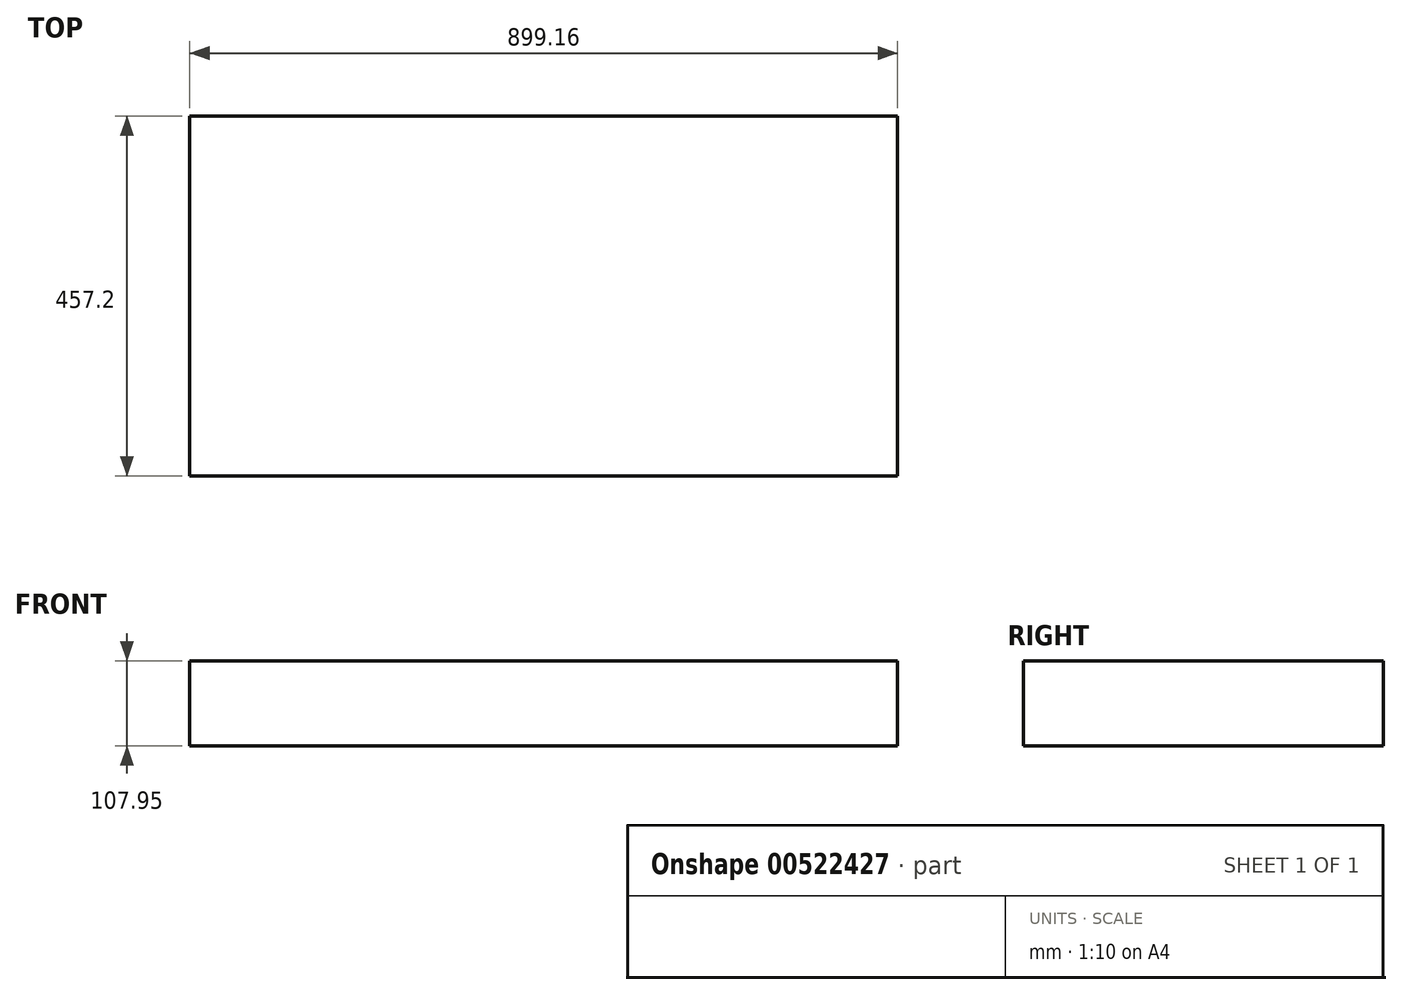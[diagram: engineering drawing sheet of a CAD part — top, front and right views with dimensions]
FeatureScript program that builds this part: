
annotation { "Feature Type Name" : "Feature", "Feature Type Description" : "" }
export const myFeature = defineFeature(function(context is Context, id is Id, definition is map)
    precondition{}
    {
        {
            var Q0;
            Q0=qCreatedBy(makeId("Top.planeOp"),FACE);
            var sketch = newSketch(context, id + "F0", { "sketchPlane" : qUnion([Q0])});
            skLineSegment(sketch, "E0.bottom", {"start": v(449.58, 228.6) * mm, "end": v(-449.58, 228.6) * mm});
            skLineSegment(sketch, "E0.top", {"start": v(449.58, -228.6) * mm, "end": v(-449.58, -228.6) * mm});
            skLineSegment(sketch, "E0.left", {"start": v(449.58, 228.6) * mm, "end": v(449.58, -228.6) * mm});
            skLineSegment(sketch, "E0.right", {"start": v(-449.58, 228.6) * mm, "end": v(-449.58, -228.6) * mm});
            skPoint(sketch, "E0.middle", {"position": v(0, 0) * mm});
            skSolve(sketch);
        }
        {
            var Q0;
            Q0=makeQuery(id+"F0.imprint","IMPRINT",FACE,{"disambiguationData":[TD([[makeQuery(id+"F0.imprint","IMPRINT",EDGE,{"derivedFrom":sQuery(id+"F0.wireOp",EDGE,"E0.bottom")}),1.0]])]});
            extrude(context, id + "F1", {"entities" : qUnion([Q0]), "depth" : 107.95 * mm, "offsetDistance" : 25.4 * mm});
        }
    });
